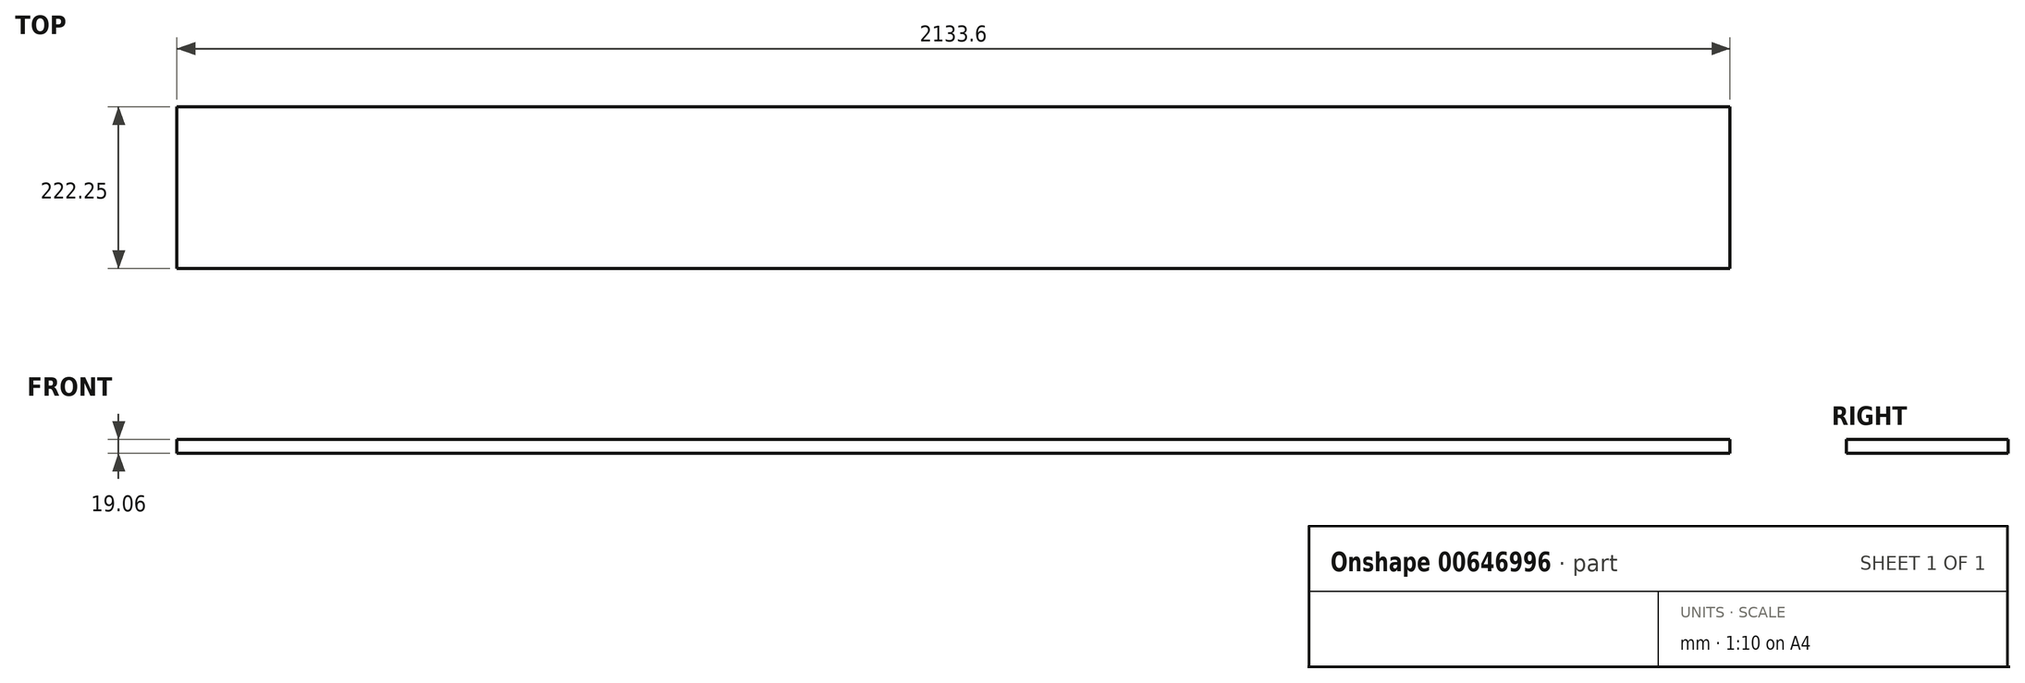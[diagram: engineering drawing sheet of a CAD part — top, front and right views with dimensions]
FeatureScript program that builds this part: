
annotation { "Feature Type Name" : "Feature", "Feature Type Description" : "" }
export const myFeature = defineFeature(function(context is Context, id is Id, definition is map)
    precondition{}
    {
        {
            var Q0;
            Q0=qCreatedBy(makeId("Top.planeOp"),FACE);
            var sketch = newSketch(context, id + "F0", { "sketchPlane" : qUnion([Q0])});
            skLineSegment(sketch, "E0.bottom", {"start": v(-961.28, 113.5) * mm, "end": v(1172.32, 113.5) * mm});
            skLineSegment(sketch, "E0.top", {"start": v(-961.28, -108.76) * mm, "end": v(1172.32, -108.76) * mm});
            skLineSegment(sketch, "E0.left", {"start": v(-961.28, 113.5) * mm, "end": v(-961.28, -108.76) * mm});
            skLineSegment(sketch, "E0.right", {"start": v(1172.32, 113.5) * mm, "end": v(1172.32, -108.76) * mm});
            skSolve(sketch);
        }
        {
            var Q0;
            Q0=makeQuery(id+"F0.imprint","IMPRINT",FACE,{"disambiguationData":[TD([[makeQuery(id+"F0.imprint","IMPRINT",EDGE,{"derivedFrom":sQuery(id+"F0.wireOp",EDGE,"E0.bottom")}),-1.0]])]});
            extrude(context, id + "F1", {"entities" : qUnion([Q0]), "endBound" : BoundingType.SYMMETRIC, "depth" : 19.05 * mm, "offsetDistance" : 25.4 * mm});
        }
    });
